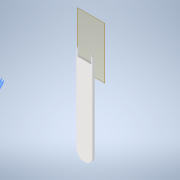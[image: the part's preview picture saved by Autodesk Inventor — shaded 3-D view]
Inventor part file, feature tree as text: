
AUTODESK INVENTOR PART (.ipt)
format: ipt  version: 2022 (Build 260153000, 153)  size: 104,960 bytes
history: native  units: mm
features: reference x4, other x2, plane x1, extrude x1, sketch x1
ambient origin geometry x8: Origin, YZ Plane, XZ Plane, XY Plane, X Axis, Y Axis, Z Axis, Center Point
bodies: Solid1 (feature_tree)
feature tree (9):
  plane  "Work Plane1"
  extrude  "Extrusion1"  Depth=3.3mm
  sketch  "Sketch1"  dims[d1=24.0mm d2=10.5mm d4=6.3mm d6=24.0mm d7=3.3mm d8=0.0mm]
  reference  "Reference1"
  reference  "Reference2"
  reference  "Reference3"
  reference  "Reference4"
  other  "Assembly2"
  other  "BaseMotoresHombrp:1"
